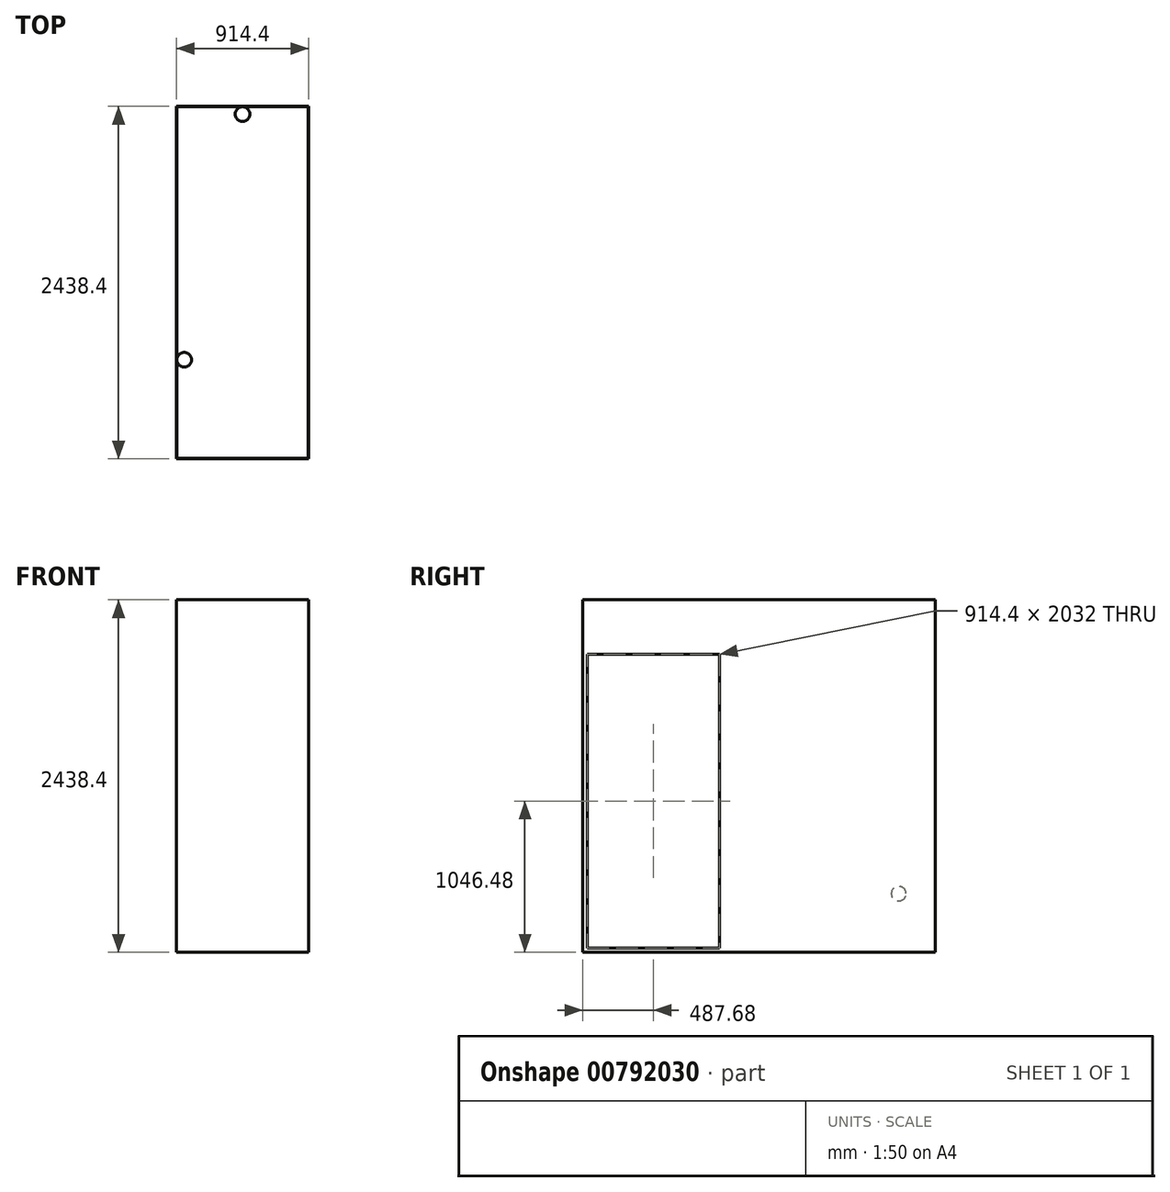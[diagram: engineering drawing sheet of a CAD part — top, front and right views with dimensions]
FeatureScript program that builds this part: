
annotation { "Feature Type Name" : "Feature", "Feature Type Description" : "" }
export const myFeature = defineFeature(function(context is Context, id is Id, definition is map)
    precondition{}
    {
        {
            var Q0;
            Q0=qCreatedBy(makeId("Top.planeOp"),FACE);
            var sketch = newSketch(context, id + "F0", { "sketchPlane" : qUnion([Q0])});
            skLineSegment(sketch, "E0.bottom", {"start": v(0, 0) * mm, "end": v(914.4, 0) * mm});
            skLineSegment(sketch, "E0.top", {"start": v(0, 2438.4) * mm, "end": v(914.4, 2438.4) * mm});
            skLineSegment(sketch, "E0.left", {"start": v(0, 0) * mm, "end": v(0, 2438.4) * mm});
            skLineSegment(sketch, "E0.right", {"start": v(914.4, 0) * mm, "end": v(914.4, 2438.4) * mm});
            skSolve(sketch);
        }
        {
            var Q0;
            Q0 = qSketchRegion(id + "F0", true);
            extrude(context, id + "F1", {"entities" : qUnion([Q0]), "depth" : 2438.4 * mm, "offsetDistance" : 30.48 * mm});
        }
        {
            var Q0;
            Q0=makeQuery(id+"F1.opExtrude","CAP_FACE",FACE,{"disambiguationData":[OSD([sQuery(id+"F0.wireOp",EDGE,"E0.bottom"),sQuery(id+"F0.wireOp",EDGE,"E0.top"),sQuery(id+"F0.wireOp",EDGE,"E0.left"),sQuery(id+"F0.wireOp",EDGE,"E0.right")])],"isStart":false});
            shell(context, id + "F2", {"entities" : qUnion([Q0]), "thickness" : 3.05 * mm});
        }
        {
            var Q0;
            Q0=makeQuery(id+"F1.opExtrude","CAP_FACE",FACE,{"disambiguationData":[OSD([sQuery(id+"F0.wireOp",EDGE,"E0.bottom"),sQuery(id+"F0.wireOp",EDGE,"E0.top"),sQuery(id+"F0.wireOp",EDGE,"E0.left"),sQuery(id+"F0.wireOp",EDGE,"E0.right")])],"isStart":true});
            var sketch = newSketch(context, id + "F3", { "sketchPlane" : qUnion([Q0])});
            skCircle(sketch, "E1", {"center": v(457.2, -2384.55) * mm, "radius": 50.8 * mm});
            skLineSegment(sketch, "E2", {"start": v(457.2, -2384.55) * mm, "end": v(914.4, -2384.55) * mm, "construction": true});
            skCircle(sketch, "E3", {"center": v(53.85, -685.8) * mm, "radius": 50.8 * mm});
            skLineSegment(sketch, "E4", {"start": v(53.85, -685.8) * mm, "end": v(53.85, 0) * mm, "construction": true});
            skLineSegment(sketch, "E5", {"start": v(3.05, -685.8) * mm, "end": v(0, -685.8) * mm, "construction": true});
            skLineSegment(sketch, "E6", {"start": v(457.2, -2435.35) * mm, "end": v(457.2, -2438.4) * mm, "construction": true});
            skSolve(sketch);
        }
        {
            var Q0;
            Q0 = qSketchRegion(id + "F3", true);
            extrude(context, id + "F4", {"entities" : qUnion([Q0]), "operationType" : NewBodyOperationType.REMOVE, "oppositeDirection" : true, "depth" : 914.4 * mm, "offsetDistance" : 30.48 * mm});
        }
        {
            var Q0;
            Q0=makeQuery(id+"F1.opExtrude","SWEPT_FACE",FACE,{"disambiguationData":[OSD([sQuery(id+"F0.wireOp",EDGE,"E0.left")])]});
            var sketch = newSketch(context, id + "F5", { "sketchPlane" : qUnion([Q0])});
            skCircle(sketch, "E7", {"center": v(-2184.4, 406.4) * mm, "radius": 50.8 * mm});
            skLineSegment(sketch, "E8", {"start": v(-2184.4, 406.4) * mm, "end": v(-2438.4, 406.4) * mm, "construction": true});
            skLineSegment(sketch, "E9", {"start": v(-2184.4, 406.4) * mm, "end": v(-2184.4, 0) * mm, "construction": true});
            skSolve(sketch);
        }
        {
            var Q0;
            Q0 = qSketchRegion(id + "F5", true);
            extrude(context, id + "F6", {"entities" : qUnion([Q0]), "operationType" : NewBodyOperationType.REMOVE, "oppositeDirection" : true, "depth" : 30.48 * mm, "offsetDistance" : 30.48 * mm});
        }
        {
            var Q0;
            Q0=makeQuery(id+"F1.opExtrude","SWEPT_FACE",FACE,{"disambiguationData":[OSD([sQuery(id+"F0.wireOp",EDGE,"E0.right")])]});
            var sketch = newSketch(context, id + "F7", { "sketchPlane" : qUnion([Q0])});
            skLineSegment(sketch, "E10.bottom", {"start": v(30.48, 30.48) * mm, "end": v(944.88, 30.48) * mm});
            skLineSegment(sketch, "E10.top", {"start": v(30.48, 2062.48) * mm, "end": v(944.88, 2062.48) * mm});
            skLineSegment(sketch, "E10.left", {"start": v(30.48, 30.48) * mm, "end": v(30.48, 2062.48) * mm});
            skLineSegment(sketch, "E10.right", {"start": v(944.88, 30.48) * mm, "end": v(944.88, 2062.48) * mm});
            skLineSegment(sketch, "E11", {"start": v(30.48, 956.07) * mm, "end": v(0, 956.07) * mm, "construction": true});
            skLineSegment(sketch, "E12", {"start": v(487.68, 30.48) * mm, "end": v(487.68, 0) * mm, "construction": true});
            skSolve(sketch);
        }
        {
            var Q0;
            Q0 = qSketchRegion(id + "F7", true);
            extrude(context, id + "F8", {"entities" : qUnion([Q0]), "operationType" : NewBodyOperationType.REMOVE, "oppositeDirection" : true, "depth" : 30.48 * mm, "offsetDistance" : 30.48 * mm});
        }
    });
